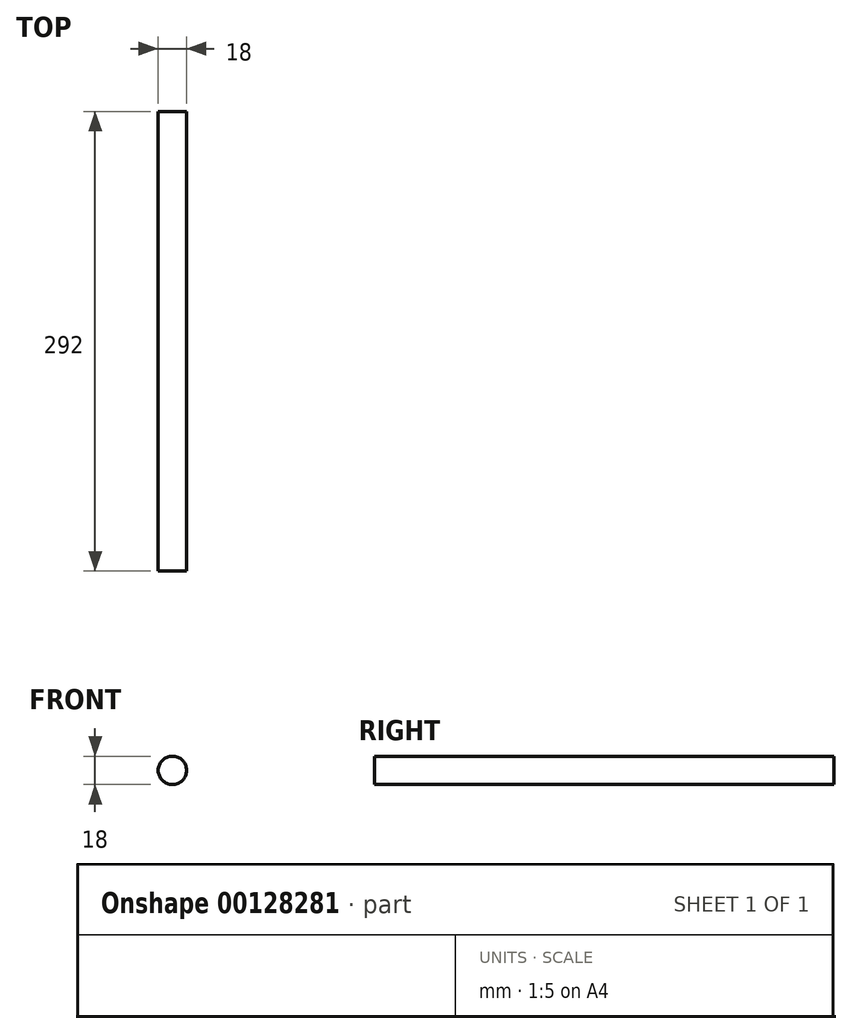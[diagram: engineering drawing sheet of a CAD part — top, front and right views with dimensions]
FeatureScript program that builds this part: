
annotation { "Feature Type Name" : "Feature", "Feature Type Description" : "" }
export const myFeature = defineFeature(function(context is Context, id is Id, definition is map)
    precondition{}
    {
        {
            var Q0;
            Q0=qCreatedBy(makeId("Front.planeOp"),FACE);
            cPlane(context, id + "F0", {"entities" : qUnion([Q0]), "cplaneType" : CPlaneType.OFFSET, "offset" : 25 * mm, "width" : 150 * mm, "height" : 150 * mm});
        }
        {
            var Q0;
            Q0=qCreatedBy(id+"F0.planeOp",FACE);
            var sketch = newSketch(context, id + "F1", { "sketchPlane" : qUnion([Q0])});
            skCircle(sketch, "E0", {"center": v(0, 0) * mm, "radius": 9 * mm});
            skSolve(sketch);
        }
        {
            var Q0;
            Q0 = qSketchRegion(id + "F1", true);
            extrude(context, id + "F2", {"entities" : qUnion([Q0]), "oppositeDirection" : true, "depth" : 292 * mm});
        }
    });
